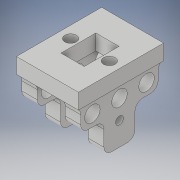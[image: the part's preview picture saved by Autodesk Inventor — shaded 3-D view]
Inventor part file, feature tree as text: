
AUTODESK INVENTOR PART (.ipt)
format: ipt  version: 2019 (Build 230136000, 136)  size: 258,048 bytes
history: native  units: mm
features: extrude x8, sketch x8, fillet x4, hole x1
ambient origin geometry x8: Origin, YZ Plane, XZ Plane, XY Plane, X Axis, Y Axis, Z Axis, Center Point
bodies: Solid1 (feature_tree)
feature tree (21):
  extrude  "Extrusion1"  Depth=80.0mm
  extrude  "Extrusion2"  Depth=30.0mm
  hole  "Hole1"  [1 undecoded]
  extrude  "Extrusion3"  Depth=20.0mm
  fillet  "Fillet1"  Radius=2.0mm
  fillet  "Fillet3"  Radius=30.0mm
  extrude  "Extrusion4"  Depth=15.0mm
  sketch  "Sketch6"  dims[d20=15.0mm d21=25.0mm]
  extrude  "Extrusion6"  Depth=25.0mm
  extrude  "Extrusion7"  Depth=15.0mm TaperAngle=0.0deg
  extrude  "Extrusion8"  Depth=10.0mm
  extrude  "Extrusion9"  Depth=45.0mm
  fillet  "Fillet7"  Radius=30.0mm
  fillet  "Fillet8"  Radius=20.0mm
  sketch  "Sketch1"  dims[d0=110.0mm d1=80.0mm]
  sketch  "Sketch2"  dims[d2=20.0mm d3=0.0mm d4=30.0mm]
  sketch  "Sketch3"  dims[d5=20.0mm d6=20.0mm]
  sketch  "Sketch4"  dims[d7=2.0mm d8=20.0mm d9=2.0mm d10=30.0mm d11=0.0mm]
  sketch  "Sketch5"  dims[d12=20.0mm d13=6.0mm d14=4.0mm d15=2.0mm d16=90.0deg d17=15.0mm d18=20.594885mm d19=15.0mm]
  sketch  "Sketch7"  dims[d23=25.0mm d24=15.0mm d25=0.0mm]
  sketch  "Sketch9"  dims[d26=10.0mm d28=10.0mm d30=45.0mm d31=30.0mm d32=20.0mm d33=0.0mm d37=70.0mm d38=0.0mm d39=70.0mm d40=0.0mm d42=20.0mm d43=15.0mm d44=100.0mm d45=0.0mm d46=10.0mm d47=10.0mm d48=100.0mm d49=0.0mm d50=10.0mm d51=10.0mm d22=0.75mm]
note: 1 required parameter value undecoded (feature->parameter linkage not recoverable at this tier; creation-order binding heuristic only, values carry confidence <= 0.55)
